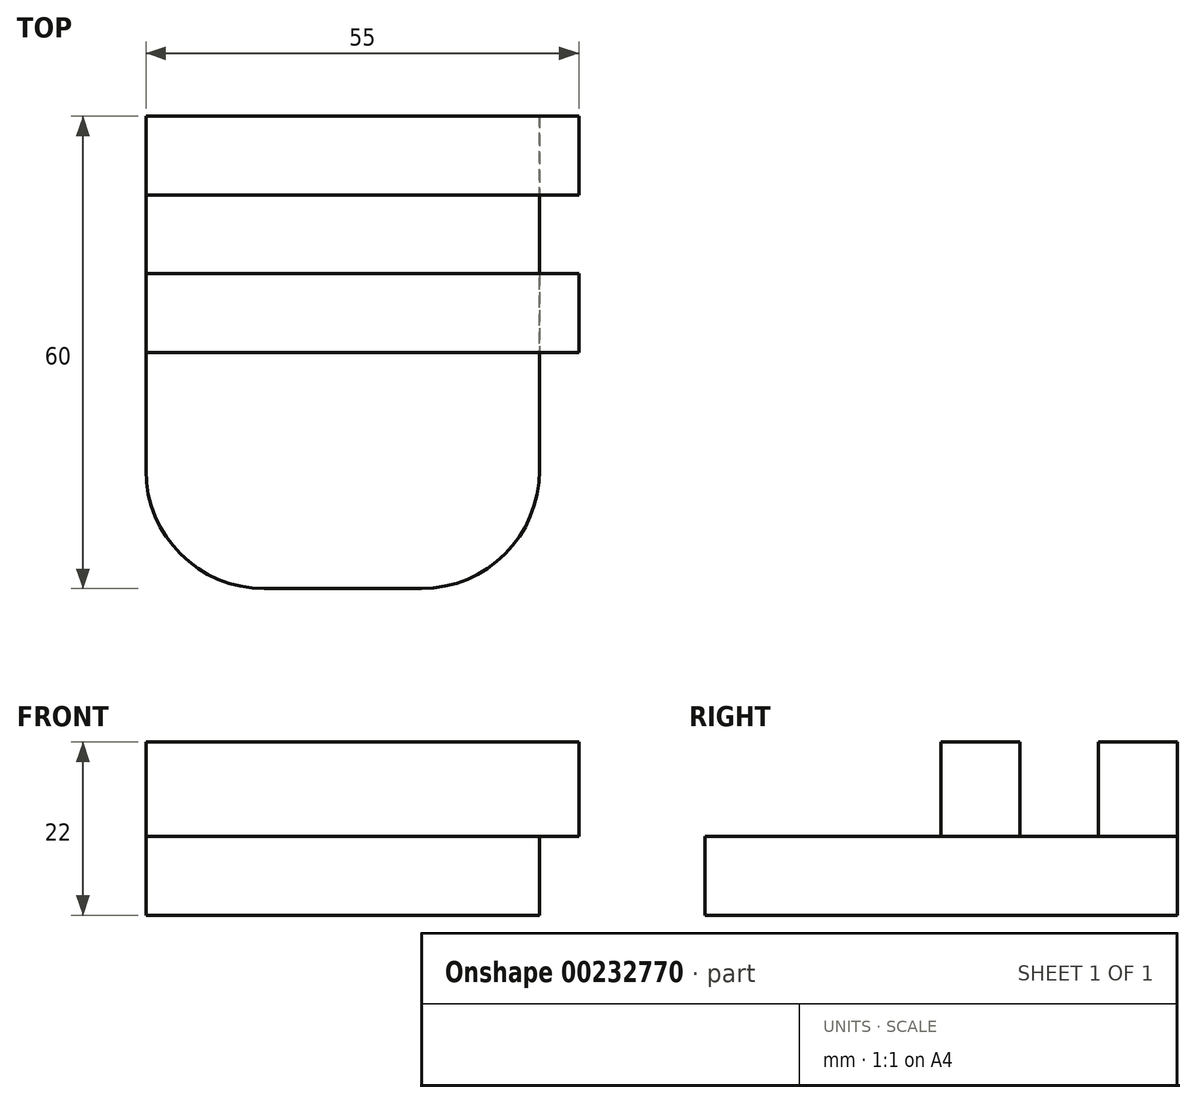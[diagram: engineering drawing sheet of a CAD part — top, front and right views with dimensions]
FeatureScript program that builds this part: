
annotation { "Feature Type Name" : "Feature", "Feature Type Description" : "" }
export const myFeature = defineFeature(function(context is Context, id is Id, definition is map)
    precondition{}
    {
        {
            var Q0;
            Q0=qCreatedBy(makeId("Top.planeOp"),FACE);
            var sketch = newSketch(context, id + "F0", { "sketchPlane" : qUnion([Q0])});
            skLineSegment(sketch, "E0", {"start": v(0, 30) * mm, "end": v(0, -15) * mm});
            skLineSegment(sketch, "E1", {"start": v(15, -30) * mm, "end": v(35, -30) * mm});
            skLineSegment(sketch, "E2", {"start": v(50, -15) * mm, "end": v(50, 0) * mm});
            skLineSegment(sketch, "E3", {"start": v(50, 0) * mm, "end": v(55, 0) * mm});
            skLineSegment(sketch, "E4", {"start": v(55, 0) * mm, "end": v(55, 30) * mm});
            skLineSegment(sketch, "E5", {"start": v(55, 30) * mm, "end": v(0, 30) * mm});
            skArc(sketch, "E6", {"start": v(35, -30) * mm, "mid": v(45.6, -25.6) * mm, "end": v(50, -15) * mm});
            skArc(sketch, "E7", {"start": v(0, -15) * mm, "mid": v(4.4, -25.6) * mm, "end": v(15, -30) * mm});
            skSolve(sketch);
        }
        {
            var Q0;
            Q0=makeQuery(id+"F0.imprint","IMPRINT",FACE,{"disambiguationData":[TD([[makeQuery(id+"F0.imprint","IMPRINT",EDGE,{"derivedFrom":sQuery(id+"F0.wireOp",EDGE,"E0")}),1.0]])]});
            extrude(context, id + "F1", {"entities" : qUnion([Q0]), "depth" : 10 * mm});
        }
        {
            var Q0;
            Q0=makeQuery(id+"F1.opExtrude","CAP_FACE",FACE,{"disambiguationData":[OSD([sQuery(id+"F0.wireOp",EDGE,"E0"),sQuery(id+"F0.wireOp",EDGE,"E1"),sQuery(id+"F0.wireOp",EDGE,"E2"),sQuery(id+"F0.wireOp",EDGE,"E3"),sQuery(id+"F0.wireOp",EDGE,"E4"),sQuery(id+"F0.wireOp",EDGE,"E5"),sQuery(id+"F0.wireOp",EDGE,"E6"),sQuery(id+"F0.wireOp",EDGE,"E7")])],"isStart":false});
            var sketch = newSketch(context, id + "F2", { "sketchPlane" : qUnion([Q0])});
            skLineSegment(sketch, "E8.0.0", {"start": v(50, -15) * mm, "end": v(50, 0) * mm});
            skLineSegment(sketch, "E8.0.1", {"start": v(50, 0) * mm, "end": v(55, 0) * mm});
            skLineSegment(sketch, "E8.0.2", {"start": v(55, 0) * mm, "end": v(55, 30) * mm});
            skLineSegment(sketch, "E8.0.3", {"start": v(55, 30) * mm, "end": v(0, 30) * mm});
            skLineSegment(sketch, "E8.0.4", {"start": v(0, 30) * mm, "end": v(0, -15) * mm});
            skArc(sketch, "E8.0.5", {"start": v(0, -15) * mm, "mid": v(4.4, -25.6) * mm, "end": v(15, -30) * mm});
            skLineSegment(sketch, "E8.0.6", {"start": v(15, -30) * mm, "end": v(35, -30) * mm});
            skArc(sketch, "E8.0.7", {"start": v(35, -30) * mm, "mid": v(45.6, -25.6) * mm, "end": v(50, -15) * mm});
            skLineSegment(sketch, "E9", {"start": v(50, 0) * mm, "end": v(0, 0) * mm});
            skLineSegment(sketch, "E10", {"start": v(0, 0) * mm, "end": v(0, 10) * mm});
            skLineSegment(sketch, "E11", {"start": v(0, 10) * mm, "end": v(55, 10) * mm});
            skLineSegment(sketch, "E12", {"start": v(55, 10) * mm, "end": v(55, 0) * mm});
            skLineSegment(sketch, "E13", {"start": v(0, 30) * mm, "end": v(0, 20) * mm});
            skLineSegment(sketch, "E14", {"start": v(0, 20) * mm, "end": v(55, 20) * mm});
            skLineSegment(sketch, "E15", {"start": v(55, 20) * mm, "end": v(55, 30) * mm});
            skSolve(sketch);
        }
        {
            var Q0;
            Q0=makeQuery(id+"F2.imprint","IMPRINT",FACE,{"disambiguationData":[TD([[makeQuery(id+"F2.imprint","IMPRINT",EDGE,{"derivedFrom":sQuery(id+"F2.wireOp",EDGE,"E8.0.3")}),1.0]])]});
            var Q1;
            Q1=makeQuery(id+"F2.imprint","IMPRINT",FACE,{"disambiguationData":[TD([[makeQuery(id+"F2.imprint","IMPRINT",EDGE,{"derivedFrom":sQuery(id+"F2.wireOp",EDGE,"E8.0.1")}),1.0]])]});
            extrude(context, id + "F3", {"entities" : qUnion([Q0, Q1]), "operationType" : NewBodyOperationType.ADD, "depth" : 12 * mm});
        }
        {
            var Q0;
            Q0=makeQuery(id+"F3.boolean.opBoolean","MERGE",FACE,{"derivedFrom":[makeQuery(id+"F1.opExtrude","SWEPT_FACE",FACE,{"disambiguationData":[OSD([sQuery(id+"F0.wireOp",EDGE,"E3")])]}),makeQuery(id+"F3.opExtrude","SWEPT_FACE",FACE,{"disambiguationData":[OSD([sQuery(id+"F2.wireOp",EDGE,"E8.0.1"),sQuery(id+"F2.wireOp",EDGE,"E9")])]})]});
            var sketch = newSketch(context, id + "F4", { "sketchPlane" : qUnion([Q0])});
            skLineSegment(sketch, "E16.0.0", {"start": v(50, 0) * mm, "end": v(55, 0) * mm});
            skLineSegment(sketch, "E16.0.1", {"start": v(55, 0) * mm, "end": v(55, 22) * mm});
            skLineSegment(sketch, "E16.0.2", {"start": v(55, 22) * mm, "end": v(0, 22) * mm});
            skLineSegment(sketch, "E16.0.3", {"start": v(0, 22) * mm, "end": v(0, 10) * mm});
            skLineSegment(sketch, "E16.0.4", {"start": v(0, 10) * mm, "end": v(50, 10) * mm});
            skLineSegment(sketch, "E16.0.5", {"start": v(50, 10) * mm, "end": v(50, 0) * mm});
            skLineSegment(sketch, "E17", {"start": v(50, 10) * mm, "end": v(55, 10) * mm});
            skLineSegment(sketch, "E18", {"start": v(55, 10) * mm, "end": v(55, 0) * mm});
            skLineSegment(sketch, "E19", {"start": v(50, 0) * mm, "end": v(50, 10) * mm});
            skSolve(sketch);
        }
        {
            var Q0;
            Q0=makeQuery(id+"F4.imprint","IMPRINT",FACE,{"disambiguationData":[TD([[makeQuery(id+"F4.imprint","IMPRINT",EDGE,{"derivedFrom":sQuery(id+"F4.wireOp",EDGE,"E16.0.0")}),1.0]])]});
            extrude(context, id + "F5", {"entities" : qUnion([Q0]), "operationType" : NewBodyOperationType.REMOVE, "endBound" : BoundingType.THROUGH_ALL, "oppositeDirection" : true, "depth" : 25 * mm});
        }
    });
